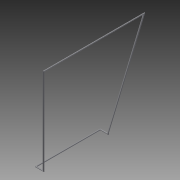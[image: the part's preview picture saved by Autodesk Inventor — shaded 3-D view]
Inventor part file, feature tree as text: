
AUTODESK INVENTOR PART (.ipt)
format: ipt  version: 2013 (Build 170138000, 138)  size: 161,280 bytes
history: native  units: in
note: dims shown in document units (in); Inventor stores cm internally (conversion verified against a paired STEP export)
features: extrude x6, sketch x6, fillet x2
ambient origin geometry x8: Origin, YZ Plane, XZ Plane, XY Plane, X Axis, Y Axis, Z Axis, Center Point
bodies: Solid1 (feature_tree)
feature tree (14):
  extrude  "Extrusion1"  Depth=15.0in
  extrude  "Extrusion2"  Depth=0.25in
  extrude  "Extrusion3"  Depth=1.5in TaperAngle=0.0deg
  extrude  "Extrusion5"  Depth=20.0in
  extrude  "Extrusion6"  Depth=0.25in
  extrude  "Extrusion7"  Depth=14.5in TaperAngle=0.0deg
  fillet  "Fillet2"  Radius=8.5in
  fillet  "Fillet3"  Radius=20.0in
  sketch  "Sketch1"  dims[d0=0.25in d1=15.0in]
  sketch  "Sketch2"  dims[d2=0.25in d3=0.0in d4=0.25in]
  sketch  "Sketch3"  dims[d5=0.25in d6=1.5in d7=0.0in]
  sketch  "Sketch5"  dims[d8=0.25in d9=20.0in]
  sketch  "Sketch7"  dims[d10=0.25in d11=0.0in d16=0.25in]
  sketch  "Sketch8"  dims[d17=0.25in d18=14.5in d19=0.0in d21=8.5in d22=0.0in d23=20.0in d25=8.5in d27=0.25in d28=90.0deg d29=0.25in d30=180.0deg d31=0.25in d32=0.0in d33=0.125in d34=0.125in]
